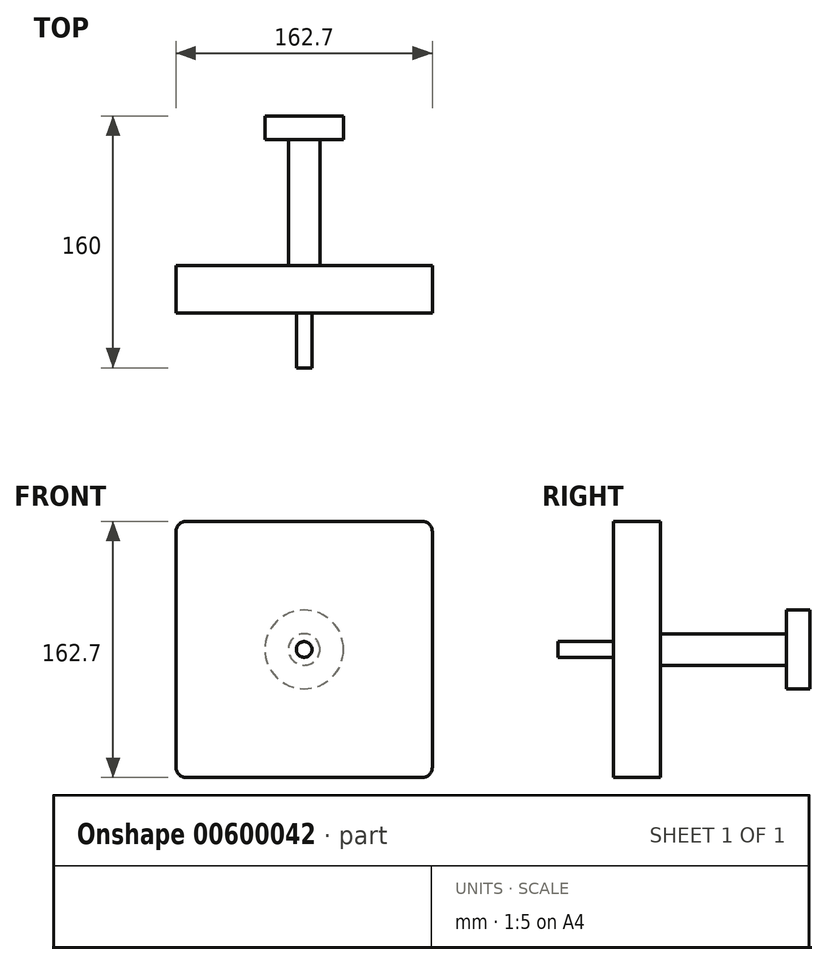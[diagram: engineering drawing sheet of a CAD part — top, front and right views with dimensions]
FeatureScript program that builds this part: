
annotation { "Feature Type Name" : "Feature", "Feature Type Description" : "" }
export const myFeature = defineFeature(function(context is Context, id is Id, definition is map)
    precondition{}
    {
        {
            var Q0;
            Q0=qCreatedBy(makeId("Front.planeOp"),FACE);
            var sketch = newSketch(context, id + "F0", { "sketchPlane" : qUnion([Q0])});
            skLineSegment(sketch, "E0.bottom", {"start": v(75, 81.35) * mm, "end": v(-75, 81.35) * mm});
            skLineSegment(sketch, "E0.top", {"start": v(75, -81.35) * mm, "end": v(-75, -81.35) * mm});
            skLineSegment(sketch, "E0.left", {"start": v(81.35, 75) * mm, "end": v(81.35, -75) * mm});
            skLineSegment(sketch, "E0.right", {"start": v(-81.35, 75) * mm, "end": v(-81.35, -75) * mm});
            skPoint(sketch, "E0.middle", {"position": v(0, 0) * mm});
            skPoint(sketch, "E1.visualSharp", {"position": v(81.35, 81.35) * mm});
            skArc(sketch, "E1.filletArc", {"start": v(81.35, 75) * mm, "mid": v(79.5, 79.5) * mm, "end": v(75, 81.35) * mm});
            skPoint(sketch, "E2.visualSharp", {"position": v(-81.35, 81.35) * mm});
            skArc(sketch, "E2.filletArc", {"start": v(-75, 81.35) * mm, "mid": v(-79.5, 79.5) * mm, "end": v(-81.35, 75) * mm});
            skPoint(sketch, "E3.visualSharp", {"position": v(-81.35, -81.35) * mm});
            skArc(sketch, "E3.filletArc", {"start": v(-81.35, -75) * mm, "mid": v(-79.5, -79.5) * mm, "end": v(-75, -81.35) * mm});
            skPoint(sketch, "E4.visualSharp", {"position": v(81.35, -81.35) * mm});
            skArc(sketch, "E4.filletArc", {"start": v(75, -81.35) * mm, "mid": v(79.5, -79.5) * mm, "end": v(81.35, -75) * mm});
            skSolve(sketch);
        }
        {
            var Q0;
            Q0 = qSketchRegion(id + "F0", true);
            extrude(context, id + "F1", {"entities" : qUnion([Q0]), "endBound" : BoundingType.SYMMETRIC, "depth" : 30 * mm, "offsetDistance" : 25.4 * mm});
        }
        {
            var Q0;
            Q0=makeQuery(id+"F1.opExtrude","CAP_FACE",FACE,{"disambiguationData":[OSD([sQuery(id+"F0.wireOp",EDGE,"E0.bottom"),sQuery(id+"F0.wireOp",EDGE,"E0.top"),sQuery(id+"F0.wireOp",EDGE,"E0.left"),sQuery(id+"F0.wireOp",EDGE,"E0.right"),sQuery(id+"F0.wireOp",EDGE,"E1.filletArc"),sQuery(id+"F0.wireOp",EDGE,"E2.filletArc"),sQuery(id+"F0.wireOp",EDGE,"E3.filletArc"),sQuery(id+"F0.wireOp",EDGE,"E4.filletArc")])],"isStart":false});
            var sketch = newSketch(context, id + "F2", { "sketchPlane" : qUnion([Q0])});
            skCircle(sketch, "E5", {"center": v(0, 0) * mm, "radius": 5 * mm});
            skLineSegment(sketch, "E6", {"start": v(-5, 0) * mm, "end": v(-5, 0) * mm});
            skLineSegment(sketch, "E7", {"start": v(5, 0) * mm, "end": v(5, 0) * mm});
            skSolve(sketch);
        }
        {
            var Q0;
            Q0 = qSketchRegion(id + "F2", true);
            extrude(context, id + "F3", {"entities" : qUnion([Q0]), "operationType" : NewBodyOperationType.ADD, "depth" : 35 * mm, "offsetDistance" : 25.4 * mm});
        }
        {
            var Q0;
            Q0=makeQuery(id+"F1.opExtrude","CAP_FACE",FACE,{"disambiguationData":[OSD([sQuery(id+"F0.wireOp",EDGE,"E0.bottom"),sQuery(id+"F0.wireOp",EDGE,"E0.top"),sQuery(id+"F0.wireOp",EDGE,"E0.left"),sQuery(id+"F0.wireOp",EDGE,"E0.right"),sQuery(id+"F0.wireOp",EDGE,"E1.filletArc"),sQuery(id+"F0.wireOp",EDGE,"E2.filletArc"),sQuery(id+"F0.wireOp",EDGE,"E3.filletArc"),sQuery(id+"F0.wireOp",EDGE,"E4.filletArc")])],"isStart":true});
            var sketch = newSketch(context, id + "F4", { "sketchPlane" : qUnion([Q0])});
            skCircle(sketch, "E8", {"center": v(0, 0) * mm, "radius": 10 * mm});
            skLineSegment(sketch, "E9", {"start": v(-10, 0) * mm, "end": v(-10, 0) * mm});
            skLineSegment(sketch, "E10", {"start": v(10, 0) * mm, "end": v(10, 0) * mm});
            skSolve(sketch);
        }
        {
            var Q0;
            Q0 = qSketchRegion(id + "F4", true);
            extrude(context, id + "F5", {"entities" : qUnion([Q0]), "operationType" : NewBodyOperationType.ADD, "depth" : 80 * mm, "offsetDistance" : 25.4 * mm});
        }
        {
            var Q0;
            Q0=makeQuery(id+"F5.opExtrude","CAP_FACE",FACE,{"disambiguationData":[OSD([sQuery(id+"F4.wireOp",EDGE,"E8")])],"isStart":false});
            var sketch = newSketch(context, id + "F6", { "sketchPlane" : qUnion([Q0])});
            skCircle(sketch, "E11", {"center": v(0, 0) * mm, "radius": 25 * mm});
            skSolve(sketch);
        }
        {
            var Q0;
            Q0 = qSketchRegion(id + "F6", true);
            extrude(context, id + "F7", {"entities" : qUnion([Q0]), "operationType" : NewBodyOperationType.ADD, "depth" : 15 * mm, "offsetDistance" : 25.4 * mm});
        }
    });
